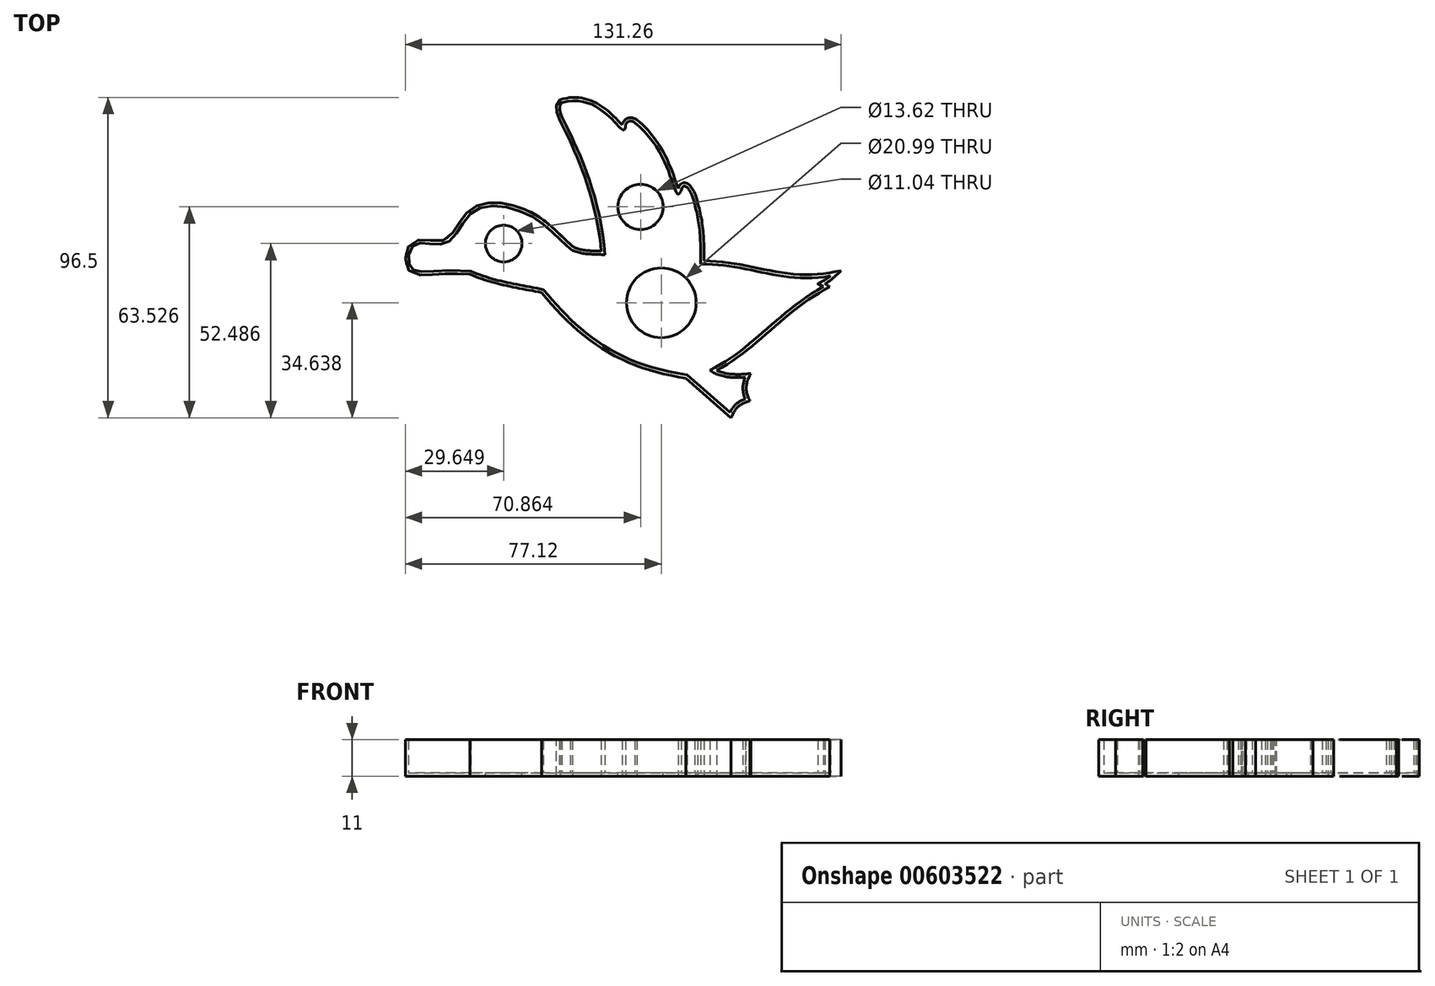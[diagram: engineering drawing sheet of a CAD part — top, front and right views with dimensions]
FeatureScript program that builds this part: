
annotation { "Feature Type Name" : "Feature", "Feature Type Description" : "" }
export const myFeature = defineFeature(function(context is Context, id is Id, definition is map)
    precondition{}
    {
        {
            var Q0;
            Q0=qCreatedBy(makeId("Top.planeOp"),FACE);
            var sketch = newSketch(context, id + "F0", { "sketchPlane" : qUnion([Q0])});
            skFitSpline(sketch, "E0", {"points": [v(-15.63, 49.63) * mm, v(2.87, 41.36) * mm, v(3.48, 42.24) * mm], "startDerivative": vector(39.5, 11.75) * mm, "endDerivative": vector(1.44, 6.1) * mm});
            skFitSpline(sketch, "E1", {"points": [v(6.33, 43.6) * mm, v(19.27, 22.05) * mm, v(20.22, 23.13) * mm], "startDerivative": vector(37.04, -29.48) * mm, "endDerivative": vector(3.82, 8.74) * mm});
            skFitSpline(sketch, "E2", {"points": [v(20.22, 23.13) * mm, v(24.27, 19) * mm], "startDerivative": vector(3.06, 12.3) * mm, "endDerivative": vector(0.17, -6.17) * mm});
            skFitSpline(sketch, "E3", {"points": [v(3.48, 42.24) * mm, v(6.33, 43.6) * mm], "startDerivative": vector(-0.9, 2.92) * mm, "endDerivative": vector(5.52, -3.9) * mm});
            skFitSpline(sketch, "E4", {"points": [v(24.27, 19) * mm, v(26.14, 0.96) * mm], "startDerivative": vector(5.47, -18.2) * mm, "endDerivative": vector(0, -17.89) * mm});
            skFitSpline(sketch, "E5", {"points": [v(26.14, 0.96) * mm, v(65.16, -2.61) * mm], "startDerivative": vector(40.8, 0.9) * mm, "endDerivative": vector(43.17, 7.58) * mm});
            skFitSpline(sketch, "E6", {"points": [v(65.16, -2.61) * mm, v(61.4, -5.02) * mm, v(63.06, -5.8) * mm], "startDerivative": vector(-8.24, -7.46) * mm, "endDerivative": vector(5.84, -3.9) * mm});
            skFitSpline(sketch, "E7", {"points": [v(63.06, -5.8) * mm, v(28.9, -30.98) * mm], "startDerivative": vector(-42.2, -23.7) * mm, "endDerivative": vector(-38.32, -18.83) * mm});
            skFitSpline(sketch, "E8", {"points": [v(28.9, -30.98) * mm, v(39.56, -33.12) * mm], "startDerivative": vector(8, -6.26) * mm, "endDerivative": vector(10.78, 1) * mm});
            skFitSpline(sketch, "E9", {"points": [v(39.56, -33.12) * mm, v(39.56, -39.64) * mm], "startDerivative": vector(-3, -6.45) * mm, "endDerivative": vector(2.89, -5.78) * mm});
            skFitSpline(sketch, "E10", {"points": [v(39.56, -39.64) * mm, v(34.95, -43.7) * mm], "startDerivative": vector(-7.95, -2.68) * mm, "endDerivative": vector(-2.48, -4.96) * mm});
            skLineSegment(sketch, "E11", {"start": v(34.95, -43.7) * mm, "end": v(22.07, -32.41) * mm});
            skFitSpline(sketch, "E12", {"points": [v(22.07, -32.41) * mm, v(-21.21, -6.73) * mm], "startDerivative": vector(-66.22, 9.55) * mm, "endDerivative": vector(-29.82, 36.1) * mm});
            skFitSpline(sketch, "E13", {"points": [v(-21.21, -6.73) * mm, v(-43.15, -1.13) * mm], "startDerivative": vector(-24.42, 5.2) * mm, "endDerivative": vector(-21.04, 9.3) * mm});
            skFitSpline(sketch, "E14", {"points": [v(-43.15, -1.13) * mm, v(-61.2, 0) * mm, v(-60.06, 6.82) * mm, v(-50.53, 7.3) * mm, v(-42.19, 16.97) * mm, v(-25.26, 15.6) * mm, v(-13.1, 5.57) * mm], "startDerivative": vector(-157.5, 17.23) * mm, "endDerivative": vector(70.32, -59.96) * mm});
            skFitSpline(sketch, "E15", {"points": [v(-13.1, 5.57) * mm, v(-2.77, 3.77) * mm], "startDerivative": vector(8.12, -5.74) * mm, "endDerivative": vector(10.2, -1.06) * mm});
            skFitSpline(sketch, "E16", {"points": [v(-2.77, 3.77) * mm, v(-14.82, 43.65) * mm, v(-15.63, 49.63) * mm], "startDerivative": vector(-4.02, 69.52) * mm, "endDerivative": vector(16.2, 16.13) * mm});
            skSolve(sketch);
        }
        {
            var Q0;
            Q0=qSketchRegion(id+"F0",true);
            extrude(context, id + "F1", {"entities" : qUnion([Q0]), "depth" : 10 * mm});
        }
        {
            var Q0;
            Q0=makeQuery(id+"F1.opExtrude","CAP_FACE",FACE,{"disambiguationData":[OSD([sQuery(id+"F0.wireOp",EDGE,"E0"),sQuery(id+"F0.wireOp",EDGE,"E1"),sQuery(id+"F0.wireOp",EDGE,"E2"),sQuery(id+"F0.wireOp",EDGE,"E3"),sQuery(id+"F0.wireOp",EDGE,"E4"),sQuery(id+"F0.wireOp",EDGE,"E5"),sQuery(id+"F0.wireOp",EDGE,"E6"),sQuery(id+"F0.wireOp",EDGE,"E7"),sQuery(id+"F0.wireOp",EDGE,"E8"),sQuery(id+"F0.wireOp",EDGE,"E9"),sQuery(id+"F0.wireOp",EDGE,"E10"),sQuery(id+"F0.wireOp",EDGE,"E11"),sQuery(id+"F0.wireOp",EDGE,"E12"),sQuery(id+"F0.wireOp",EDGE,"E13"),sQuery(id+"F0.wireOp",EDGE,"E14"),sQuery(id+"F0.wireOp",EDGE,"E15"),sQuery(id+"F0.wireOp",EDGE,"E16")])],"isStart":false});
            shell(context, id + "F2", {"entities" : qUnion([Q0]), "thickness" : 1 * mm, "oppositeDirection" : true});
        }
        {
            var Q0;
            Q0=qCreatedBy(makeId("Top.planeOp"),FACE);
            var sketch = newSketch(context, id + "F3", { "sketchPlane" : qUnion([Q0])});
            skCircle(sketch, "E17", {"center": v(-33.21, 7.18) * mm, "radius": 5.52 * mm});
            skCircle(sketch, "E18", {"center": v(14.26, -10.67) * mm, "radius": 10.5 * mm});
            skCircle(sketch, "E19", {"center": v(8, 18.22) * mm, "radius": 6.8 * mm});
            skSolve(sketch);
        }
        {
            var Q0;
            Q0=qSketchRegion(id+"F3",true);
            extrude(context, id + "F4", {"entities" : qUnion([Q0]), "operationType" : NewBodyOperationType.REMOVE, "oppositeDirection" : true, "depth" : 25 * mm});
        }
    });
